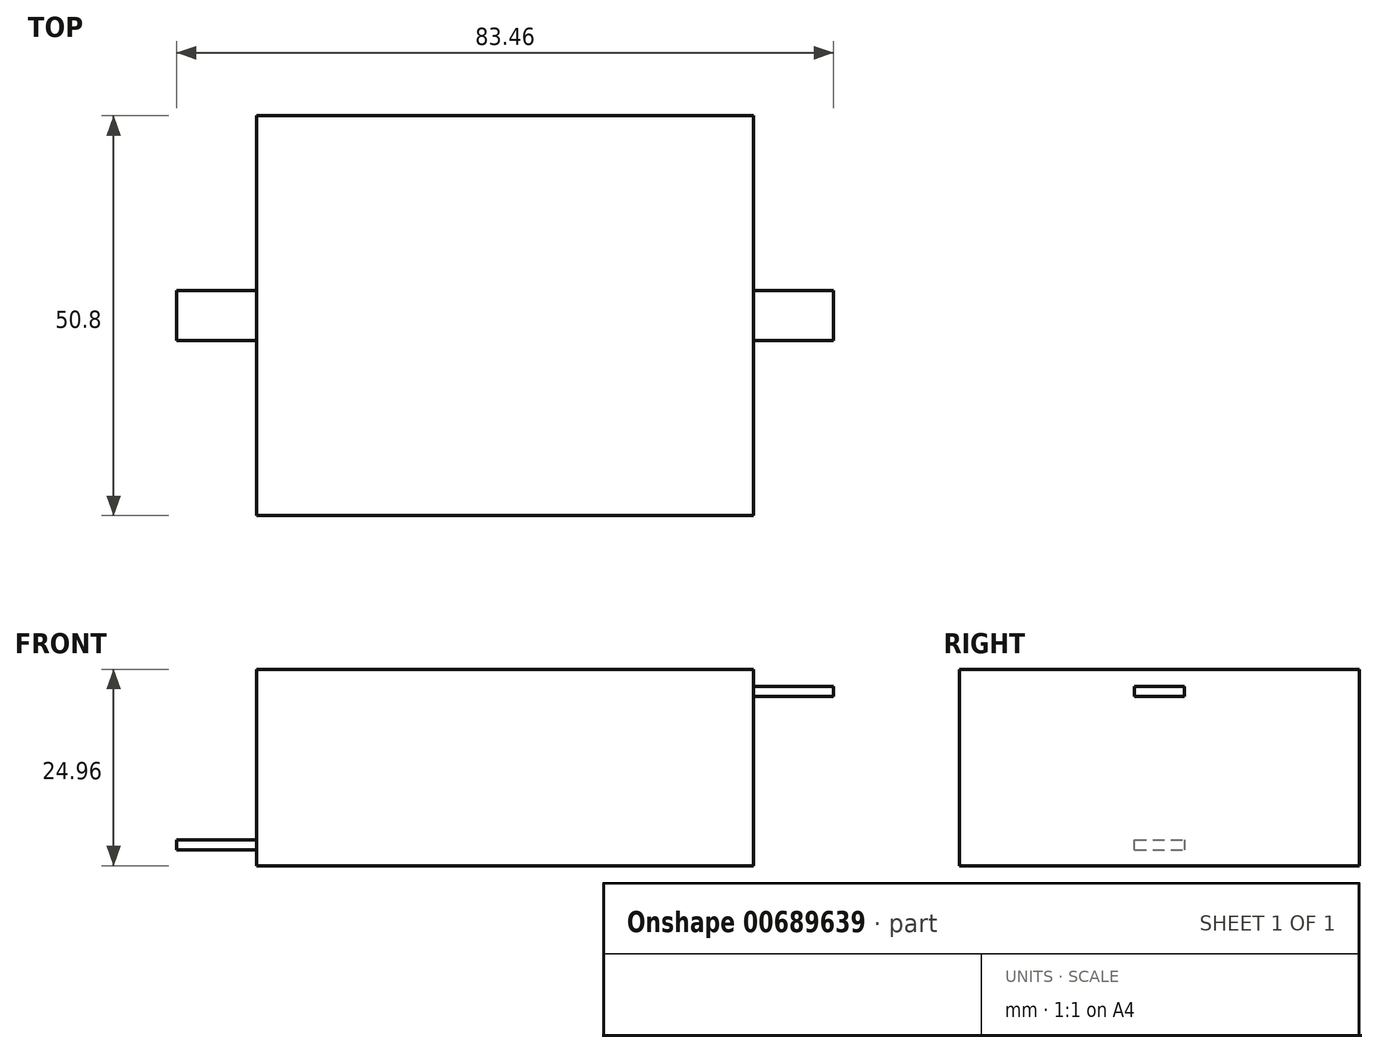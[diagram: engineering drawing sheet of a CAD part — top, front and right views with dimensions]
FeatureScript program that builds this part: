
annotation { "Feature Type Name" : "Feature", "Feature Type Description" : "" }
export const myFeature = defineFeature(function(context is Context, id is Id, definition is map)
    precondition{}
    {
        {
            var Q0;
            Q0=qCreatedBy(makeId("Front.planeOp"),FACE);
            var sketch = newSketch(context, id + "F0", { "sketchPlane" : qUnion([Q0])});
            skLineSegment(sketch, "E0.bottom", {"start": v(-31.57, 12.48) * mm, "end": v(31.57, 12.48) * mm});
            skLineSegment(sketch, "E0.top", {"start": v(-31.57, -12.48) * mm, "end": v(31.57, -12.48) * mm});
            skLineSegment(sketch, "E0.left", {"start": v(-31.57, 12.48) * mm, "end": v(-31.57, -12.48) * mm});
            skLineSegment(sketch, "E0.right", {"start": v(31.57, 12.48) * mm, "end": v(31.57, -12.48) * mm});
            skPoint(sketch, "E0.middle", {"position": v(0, 0) * mm});
            skSolve(sketch);
        }
        {
            var Q0;
            Q0=makeQuery(id+"F0.imprint","IMPRINT",FACE,{"disambiguationData":[TD([[makeQuery(id+"F0.imprint","IMPRINT",EDGE,{"derivedFrom":sQuery(id+"F0.wireOp",EDGE,"E0.bottom")}),-1.0]])]});
            var Q1;
            Q1=makeQuery(id+"F2.imprint","IMPRINT",FACE,{"disambiguationData":[TD([[makeQuery(id+"F2.imprint","IMPRINT",EDGE,{"derivedFrom":sQuery(id+"F2.wireOp",EDGE,"E1.bottom")}),-1.0]])]});
            var Q2;
            Q2=makeQuery(id+"F4.imprint","IMPRINT",FACE,{"disambiguationData":[TD([[makeQuery(id+"F4.imprint","IMPRINT",EDGE,{"derivedFrom":sQuery(id+"F4.wireOp",EDGE,"E2.bottom")}),-1.0]])]});
            extrude(context, id + "F1", {"entities" : qUnion([Q0, Q1, Q2]), "endBound" : BoundingType.SYMMETRIC, "depth" : 50.8 * mm, "offsetDistance" : 25.4 * mm});
        }
        {
            var Q0;
            Q0=qCreatedBy(makeId("Front.planeOp"),FACE);
            var sketch = newSketch(context, id + "F2", { "sketchPlane" : qUnion([Q0])});
            skLineSegment(sketch, "E1.bottom", {"start": v(31.57, 10.3) * mm, "end": v(41.73, 10.3) * mm});
            skLineSegment(sketch, "E1.top", {"start": v(31.57, 9.03) * mm, "end": v(41.73, 9.03) * mm});
            skLineSegment(sketch, "E1.left", {"start": v(31.57, 10.3) * mm, "end": v(31.57, 9.03) * mm});
            skLineSegment(sketch, "E1.right", {"start": v(41.73, 10.3) * mm, "end": v(41.73, 9.03) * mm});
            skSolve(sketch);
        }
        {
            var Q0;
            Q0 = qSketchRegion(id + "F2", true);
            extrude(context, id + "F3", {"entities" : qUnion([Q0]), "operationType" : NewBodyOperationType.ADD, "endBound" : BoundingType.SYMMETRIC, "depth" : 6.35 * mm, "offsetDistance" : 25.4 * mm});
        }
        {
            var Q0;
            Q0=qCreatedBy(makeId("Front.planeOp"),FACE);
            var sketch = newSketch(context, id + "F4", { "sketchPlane" : qUnion([Q0])});
            skLineSegment(sketch, "E2.bottom", {"start": v(-31.57, -10.47) * mm, "end": v(-41.73, -10.47) * mm});
            skLineSegment(sketch, "E2.top", {"start": v(-31.57, -9.2) * mm, "end": v(-41.73, -9.2) * mm});
            skLineSegment(sketch, "E2.left", {"start": v(-31.57, -10.47) * mm, "end": v(-31.57, -9.2) * mm});
            skLineSegment(sketch, "E2.right", {"start": v(-41.73, -10.47) * mm, "end": v(-41.73, -9.2) * mm});
            skSolve(sketch);
        }
        {
            var Q0;
            Q0 = qSketchRegion(id + "F4", true);
            extrude(context, id + "F5", {"entities" : qUnion([Q0]), "operationType" : NewBodyOperationType.ADD, "endBound" : BoundingType.SYMMETRIC, "depth" : 6.35 * mm, "offsetDistance" : 25.4 * mm});
        }
    });
